annotation { "Feature Type Name" : "Feature", "Feature Type Description" : "" }
export const myFeature = defineFeature(function(context is Context, id is Id, definition is map)
    precondition{}
    {
        {
            var Q0;
            Q0=qCreatedBy(makeId("Front.planeOp"),FACE);
            var sketch = newSketch(context, id + "F0", { "sketchPlane" : qUnion([Q0])});
            skLineSegment(sketch, "E0.bottom", {"start": v(-9.52, 63.5) * mm, "end": v(9.78, 63.5) * mm});
            skLineSegment(sketch, "E0.top", {"start": v(-9.53, -63.5) * mm, "end": v(9.78, -63.5) * mm});
            skLineSegment(sketch, "E0.left", {"start": v(-9.52, 63.5) * mm, "end": v(-9.53, -63.5) * mm});
            skLineSegment(sketch, "E0.right", {"start": v(9.53, 50.8) * mm, "end": v(9.53, -50.8) * mm});
            skPoint(sketch, "E0.middle", {"position": v(0, 0) * mm});
            skLineSegment(sketch, "E1", {"start": v(9.78, 63.5) * mm, "end": v(9.78, 50.8) * mm, "construction": true});
            skLineSegment(sketch, "E2", {"start": v(9.53, 50.8) * mm, "end": v(9.78, 50.8) * mm, "construction": true});
            skPoint(sketch, "E3.orphan", {"position": v(9.53, 63.5) * mm});
            skLineSegment(sketch, "E4", {"start": v(9.53, 50.8) * mm, "end": v(9.53, 63.5) * mm});
            skLineSegment(sketch, "E5", {"start": v(9.53, 63.5) * mm, "end": v(9.78, 63.5) * mm});
            skLineSegment(sketch, "E6", {"start": v(9.78, -50.8) * mm, "end": v(9.53, -50.8) * mm});
            skLineSegment(sketch, "E7", {"start": v(9.78, -50.8) * mm, "end": v(9.78, -63.5) * mm});
            skPoint(sketch, "E8.orphan", {"position": v(9.52, -63.5) * mm});
            skSolve(sketch);
        }
        {
            var Q0;
            Q0=qSketchRegion(id+"F0",true);
            extrude(context, id + "F1", {"entities" : qUnion([Q0]), "endBound" : BoundingType.SYMMETRIC, "depth" : 350.84 * mm, "offsetDistance" : 25.4 * mm});
        }
        {
            var Q0;
            Q0=qCreatedBy(makeId("Right.planeOp"),FACE);
            var sketch = newSketch(context, id + "F2", { "sketchPlane" : qUnion([Q0])});
            skArc(sketch, "E9", {"start": v(-175.42, -60.35) * mm, "mid": v(0, -63.5) * mm, "end": v(175.42, -60.35) * mm});
            skPoint(sketch, "E10", {"position": v(-175.42, -60.35) * mm});
            skPoint(sketch, "E11", {"position": v(175.42, -60.35) * mm});
            skLineSegment(sketch, "E12", {"start": v(-175.42, -60.35) * mm, "end": v(-175.42, -64.16) * mm});
            skLineSegment(sketch, "E13", {"start": v(-175.42, -64.16) * mm, "end": v(175.42, -64.16) * mm});
            skLineSegment(sketch, "E14", {"start": v(175.42, -64.16) * mm, "end": v(175.42, -60.35) * mm});
            skSolve(sketch);
        }
        {
            var Q0;
            Q0=makeQuery(id+"F1.opExtrude","SWEPT_FACE",FACE,{"disambiguationData":[OSD([sQuery(id+"F0.wireOp",EDGE,"E7")])]});
            var sketch = newSketch(context, id + "F3", { "sketchPlane" : qUnion([Q0])});
            skText(sketch, "E15", { "text": "SLICK TAPE", "fontName": "OpenSans-Bold.ttf"});
            const initialGuessF3  = {"E15": [-0.17377, -0.0635, 1, 0, 0.00866]};
            skSetInitialGuess(sketch, initialGuessF3);
            skSolve(sketch);
        }
        {
            var Q0;
            Q0 = qSketchRegion(id + "F3", true);
            extrude(context, id + "F4", {"entities" : qUnion([Q0]), "operationType" : NewBodyOperationType.REMOVE, "oppositeDirection" : true, "depth" : 0.25 * mm, "offsetDistance" : 25.4 * mm});
        }
    });